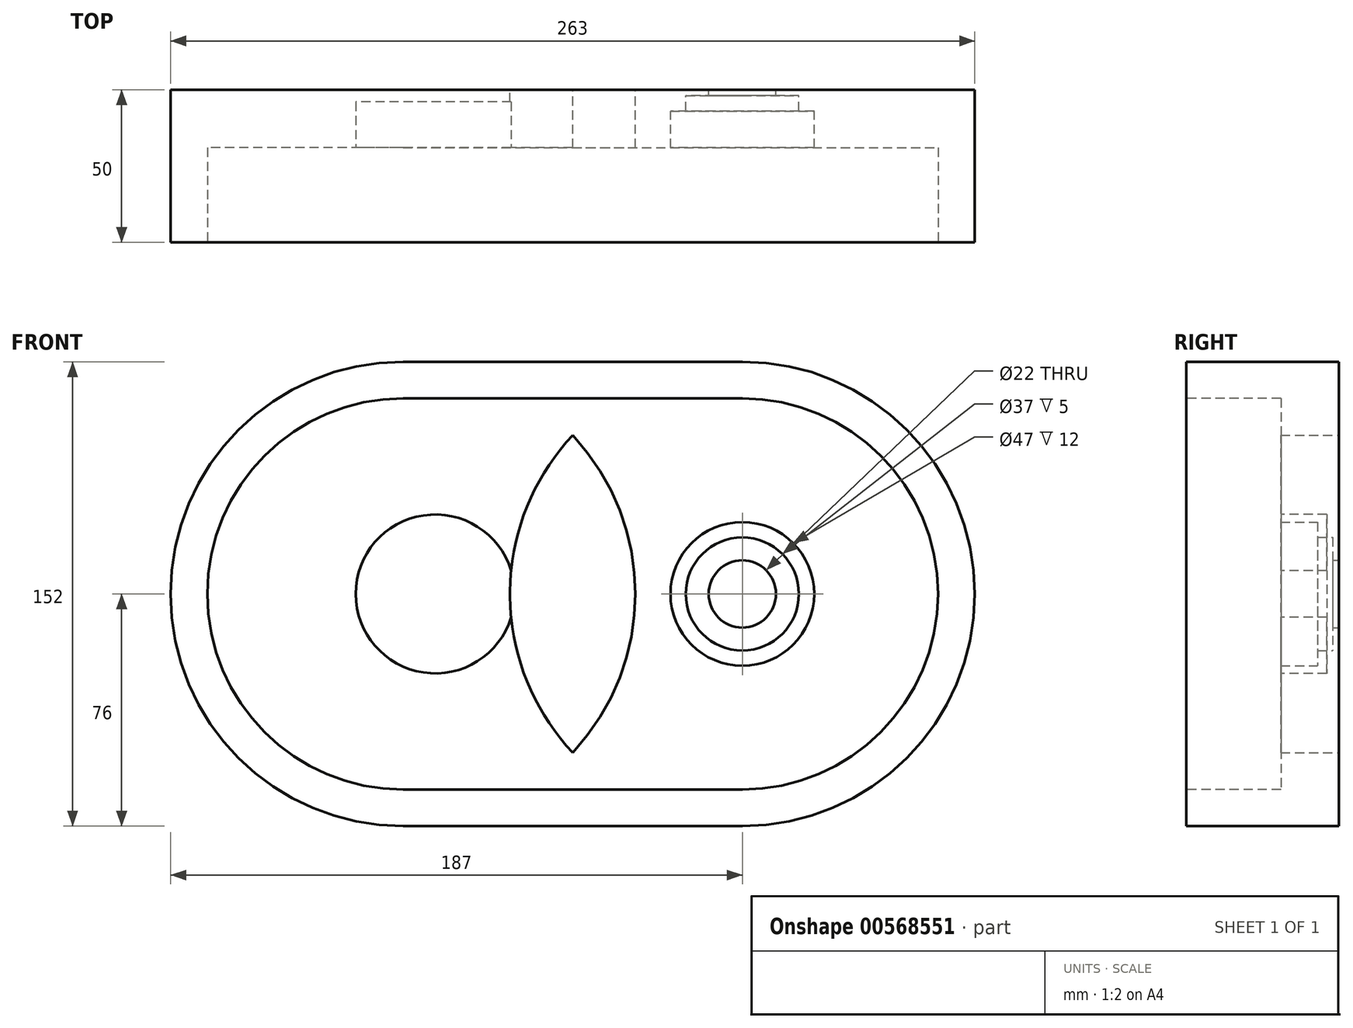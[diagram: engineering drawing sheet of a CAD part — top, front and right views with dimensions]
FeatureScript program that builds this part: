
annotation { "Feature Type Name" : "Feature", "Feature Type Description" : "" }
export const myFeature = defineFeature(function(context is Context, id is Id, definition is map)
    precondition{}
    {
        {
            var Q0;
            Q0=qCreatedBy(makeId("Front.planeOp"),FACE);
            var sketch = newSketch(context, id + "F0", { "sketchPlane" : qUnion([Q0])});
            skCircle(sketch, "E0", {"center": v(0, 0) * mm, "radius": 76 * mm});
            skCircle(sketch, "E1", {"center": v(111, 0) * mm, "radius": 76 * mm});
            skLineSegment(sketch, "E2", {"start": v(0, 76) * mm, "end": v(111, 76) * mm});
            skLineSegment(sketch, "E3", {"start": v(0, -76) * mm, "end": v(111, -76) * mm});
            skSolve(sketch);
        }
        {
            var Q0;
            Q0 = qSketchRegion(id + "F0", true);
            var Q1;
            {var subQ0=sQuery(id+"F0.wireOp",EDGE,"E1");var subQ1=sQuery(id+"F0.wireOp",EDGE,"E0");var subQ2=makeQuery(id+"F0.imprint","INTERSECT",VERTEX,{"disambiguationData":[OD(0.0)],"derivedFrom":[subQ1,subQ0]});Q1=makeQuery(id+"F0.imprint","IMPRINT",FACE,{"disambiguationData":[TD([[makeQuery(id+"F0.imprint","IMPRINT",EDGE,{"disambiguationData":[TD([[subQ2,1.0]])],"derivedFrom":subQ1}),1.0]])]});}
            extrude(context, id + "F1", {"entities" : qUnion([Q0, Q1]), "depth" : 50 * mm, "offsetDistance" : 25 * mm});
        }
        {
            var Q0;
            Q0=makeQuery(id+"F1.opExtrude","CAP_FACE",FACE,{"disambiguationData":[OSD([sQuery(id+"F0.wireOp",EDGE,"E0"),sQuery(id+"F0.wireOp",EDGE,"E1"),sQuery(id+"F0.wireOp",EDGE,"LLfFsZMf-b4Kz-KYBR-LpzR-kicHMAcoErJQ"),sQuery(id+"F0.wireOp",EDGE,"27UfcjIc-0gVm-qUQq-SDFu-eWzGSRhBPWFl")])],"isStart":false});
            var sketch = newSketch(context, id + "F2", { "sketchPlane" : qUnion([Q0])});
            skCircle(sketch, "E4", {"center": v(0, 0) * mm, "radius": 64 * mm});
            skCircle(sketch, "E5", {"center": v(111, 0) * mm, "radius": 64 * mm});
            skLineSegment(sketch, "E6", {"start": v(0, -64) * mm, "end": v(111, -64) * mm});
            skLineSegment(sketch, "E7", {"start": v(0, 64) * mm, "end": v(111, 64) * mm});
            skSolve(sketch);
        }
        {
            var Q0;
            Q0 = qSketchRegion(id + "F2", true);
            var Q1;
            {var subQ0=sQuery(id+"F2.wireOp",EDGE,"E5");var subQ1=sQuery(id+"F2.wireOp",EDGE,"E4");var subQ2=makeQuery(id+"F2.imprint","INTERSECT",VERTEX,{"disambiguationData":[OD(0.0)],"derivedFrom":[subQ1,subQ0]});Q1=makeQuery(id+"F2.imprint","IMPRINT",FACE,{"disambiguationData":[TD([[makeQuery(id+"F2.imprint","IMPRINT",EDGE,{"disambiguationData":[TD([[subQ2,1.0]])],"derivedFrom":subQ1}),1.0]])]});}
            extrude(context, id + "F3", {"entities" : qUnion([Q0, Q1]), "operationType" : NewBodyOperationType.REMOVE, "oppositeDirection" : true, "depth" : 31 * mm, "offsetDistance" : 25 * mm});
        }
        {
            var Q0;
            Q0=makeQuery(id+"F3.boolean.opBoolean","COPY",FACE,{"derivedFrom":makeQuery(id+"F3.opExtrude","CAP_FACE",FACE,{"disambiguationData":[OSD([sQuery(id+"F2.wireOp",EDGE,"E4"),sQuery(id+"F2.wireOp",EDGE,"E5"),sQuery(id+"F2.wireOp",EDGE,"E6"),sQuery(id+"F2.wireOp",EDGE,"E7")])],"isStart":false})});
            var sketch = newSketch(context, id + "F4", { "sketchPlane" : qUnion([Q0])});
            skCircle(sketch, "E8", {"center": v(10.54, 0) * mm, "radius": 26 * mm});
            skSolve(sketch);
        }
        {
            var Q0;
            Q0=makeQuery(id+"F4.imprint","IMPRINT",FACE,{"disambiguationData":[TD([[makeQuery(id+"F4.imprint","IMPRINT",EDGE,{"derivedFrom":sQuery(id+"F4.wireOp",EDGE,"E8")}),1.0]])]});
            extrude(context, id + "F5", {"entities" : qUnion([Q0]), "operationType" : NewBodyOperationType.REMOVE, "oppositeDirection" : true, "depth" : 15 * mm, "offsetDistance" : 25 * mm});
        }
        {
            var Q0;
            Q0=qCreatedBy(makeId("Right.planeOp"),FACE);
            cPlane(context, id + "F6", {"entities" : qUnion([Q0]), "cplaneType" : CPlaneType.OFFSET, "offset" : 111 * mm, "width" : 150 * mm, "height" : 150 * mm});
        }
        {
            var Q0;
            Q0=qCreatedBy(id+"F6.planeOp",FACE);
            var sketch = newSketch(context, id + "F7", { "sketchPlane" : qUnion([Q0])});
            skLineSegment(sketch, "E9", {"start": v(0, 11) * mm, "end": v(-2, 11) * mm});
            skLineSegment(sketch, "E10", {"start": v(-2, 11) * mm, "end": v(-2, 18.5) * mm});
            skLineSegment(sketch, "E11", {"start": v(-2, 18.5) * mm, "end": v(-7, 18.5) * mm});
            skLineSegment(sketch, "E12", {"start": v(-7, 18.5) * mm, "end": v(-7, 23.5) * mm});
            skLineSegment(sketch, "E13", {"start": v(-7, 23.5) * mm, "end": v(-19, 23.5) * mm});
            skLineSegment(sketch, "E14", {"start": v(-19, 23.5) * mm, "end": v(-19, 0) * mm});
            skLineSegment(sketch, "E15", {"start": v(0, 11) * mm, "end": v(0, 0) * mm});
            skLineSegment(sketch, "E16", {"start": v(0, 0) * mm, "end": v(-19, 0) * mm});
            skLineSegment(sketch, "E17", {"start": v(-56.82, 0) * mm, "end": v(22.79, 0) * mm, "construction": true});
            skPoint(sketch, "E17.endSnap0", {"position": v(-9.5, 0) * mm});
            skSolve(sketch);
        }
        {
            var Q0;
            Q0 = qSketchRegion(id + "F7", true);
            var Q1;
            Q1=sQuery(id+"F7.wireOp",EDGE,"E17");
            revolve(context, id + "F8", {"operationType" : NewBodyOperationType.REMOVE, "entities" : qUnion([Q0]), "axis" : qUnion([Q1]), "revolveType" : RevolveType.FULL, "oppositeDirection" : true});
        }
    });
